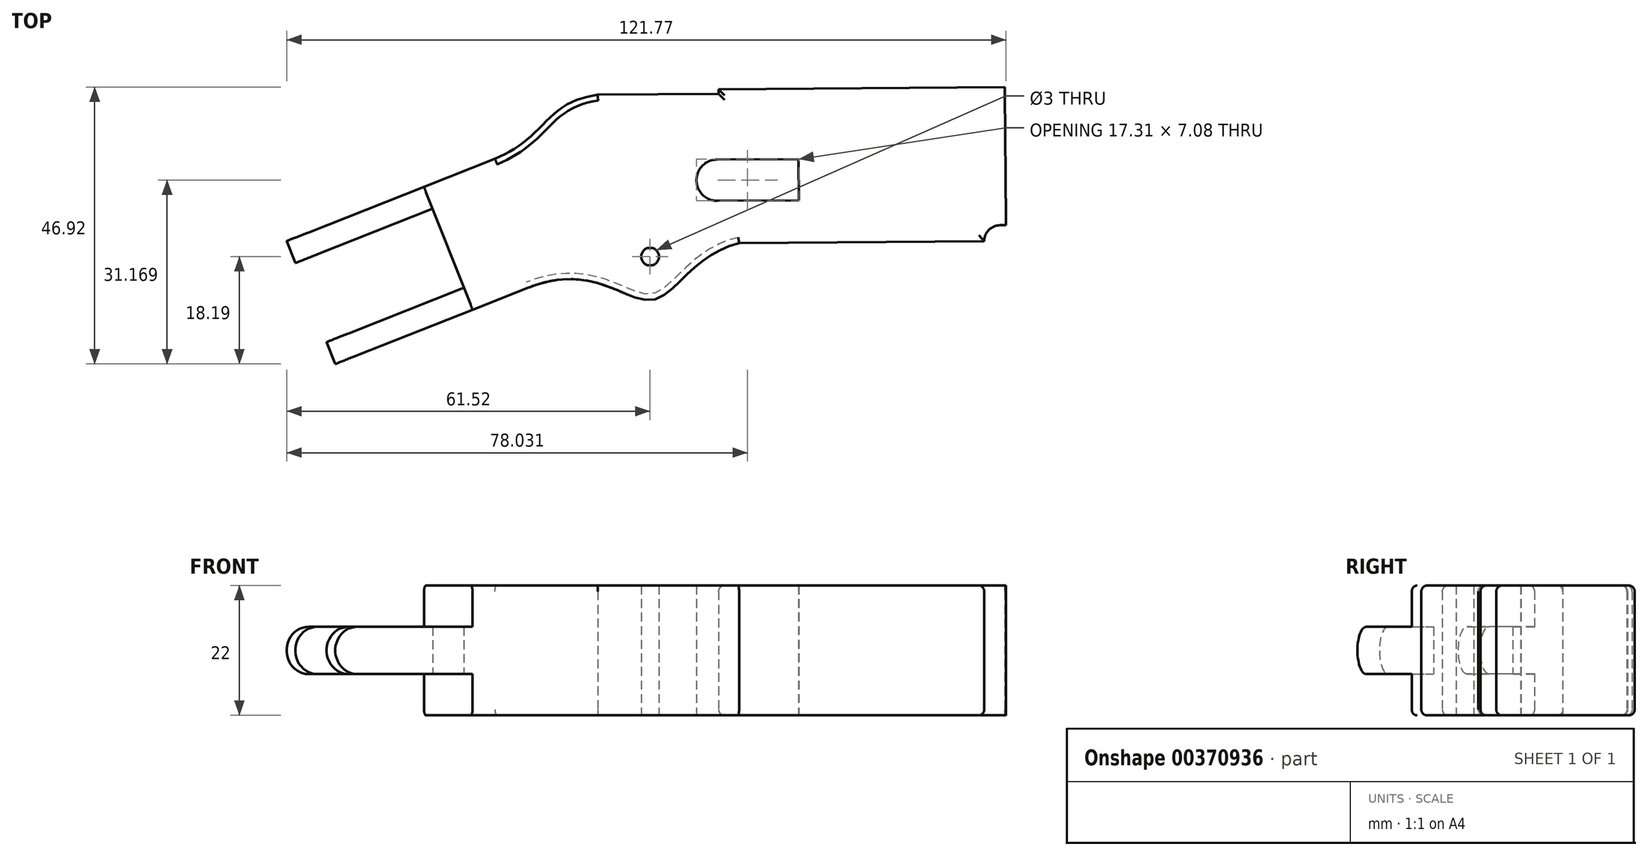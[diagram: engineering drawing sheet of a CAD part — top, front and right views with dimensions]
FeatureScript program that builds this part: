
annotation { "Feature Type Name" : "Feature", "Feature Type Description" : "" }
export const myFeature = defineFeature(function(context is Context, id is Id, definition is map)
    precondition{}
    {
        {
            var Q0;
            Q0=qCreatedBy(makeId("Top.planeOp"),FACE);
            var sketch = newSketch(context, id + "F0", { "sketchPlane" : qUnion([Q0])});
            skLineSegment(sketch, "E0", {"start": v(11.34, 16.45) * mm, "end": v(25.12, 16.52) * mm});
            skLineSegment(sketch, "E1", {"start": v(11.38, 9.44) * mm, "end": v(25.16, 9.51) * mm});
            skLineSegment(sketch, "E2", {"start": v(25.16, 9.51) * mm, "end": v(25.12, 16.52) * mm});
            skLineSegment(sketch, "E3", {"start": v(56.55, 2.63) * mm, "end": v(15.06, 2.27) * mm});
            skLineSegment(sketch, "E4", {"start": v(60.05, 28.73) * mm, "end": v(60.25, 5.31) * mm});
            skLineSegment(sketch, "E5", {"start": v(60.25, 5.31) * mm, "end": v(59.23, 5.3) * mm});
            skLineSegment(sketch, "E6", {"start": v(60.05, 28.73) * mm, "end": v(11.61, 28.3) * mm});
            skLineSegment(sketch, "E7", {"start": v(11.61, 28.3) * mm, "end": v(11.6, 27.54) * mm});
            skLineSegment(sketch, "E8", {"start": v(11.6, 27.54) * mm, "end": v(-8.88, 27.43) * mm});
            skArc(sketch, "E9", {"start": v(11.34, 16.45) * mm, "mid": v(7.86, 12.92) * mm, "end": v(11.38, 9.44) * mm});
            skFitSpline(sketch, "E10", {"points": [v(-8.88, 27.43) * mm, v(-26.26, 16.57) * mm], "startDerivative": vector(-27.72, -4.3) * mm, "endDerivative": vector(-26.55, -10.8) * mm});
            skCircle(sketch, "E11", {"center": v(0, 0) * mm, "radius": 1.5 * mm});
            skFitSpline(sketch, "E12", {"points": [v(15.06, 2.27) * mm, v(0.4, -7.32) * mm, v(-20.64, -5.27) * mm], "startDerivative": vector(-48.52, -11.19) * mm, "endDerivative": vector(-63.37, -25.45) * mm});
            skArc(sketch, "E13", {"start": v(59.23, 5.3) * mm, "mid": v(57.34, 4.51) * mm, "end": v(56.55, 2.63) * mm});
            skLineSegment(sketch, "E14", {"start": v(-20.64, -5.27) * mm, "end": v(-53.3, -18.19) * mm});
            skLineSegment(sketch, "E15", {"start": v(-61.52, 2.62) * mm, "end": v(-26.26, 16.57) * mm});
            skLineSegment(sketch, "E16", {"start": v(-61.52, 2.62) * mm, "end": v(-60.05, -1.1) * mm});
            skLineSegment(sketch, "E17", {"start": v(-53.3, -18.19) * mm, "end": v(-54.76, -14.47) * mm});
            skLineSegment(sketch, "E18", {"start": v(-60.05, -1.1) * mm, "end": v(-36.8, 8.1) * mm});
            skLineSegment(sketch, "E19", {"start": v(-36.8, 8.1) * mm, "end": v(-31.51, -5.27) * mm});
            skLineSegment(sketch, "E20", {"start": v(-31.51, -5.27) * mm, "end": v(-54.76, -14.47) * mm});
            skSolve(sketch);
        }
        {
            var Q0;
            Q0 = qSketchRegion(id + "F0", true);
            extrude(context, id + "F1", {"entities" : qUnion([Q0]), "endBound" : BoundingType.SYMMETRIC, "depth" : 22 * mm});
        }
        {
            var Q0;
            Q0=makeQuery(id+"F1.opExtrude","SWEPT_FACE",FACE,{"disambiguationData":[OSD([sQuery(id+"F0.wireOp",EDGE,"E15")])]});
            var sketch = newSketch(context, id + "F2", { "sketchPlane" : qUnion([Q0])});
            skLineSegment(sketch, "E21", {"start": v(56.24, 0) * mm, "end": v(31.24, 0) * mm, "construction": true});
            skLineSegment(sketch, "E22", {"start": v(31.24, -11.04) * mm, "end": v(31.24, 11.03) * mm});
            skLineSegment(sketch, "E23", {"start": v(31.24, -4) * mm, "end": v(52.24, -4) * mm});
            skArc(sketch, "E24", {"start": v(52.24, -4) * mm, "mid": v(55.07, -2.83) * mm, "end": v(56.24, 0) * mm});
            skLineSegment(sketch, "E25.MirrorCS", {"start": v(31.24, 4) * mm, "end": v(52.24, 4) * mm});
            skArc(sketch, "E26.MirrorCS", {"start": v(52.24, 4) * mm, "mid": v(55.07, 2.83) * mm, "end": v(56.24, 0) * mm});
            skSolve(sketch);
        }
        {
            var Q0;
            {var subQ5=sQuery(id+"F2.wireOp",EDGE,"E23");Q0=makeQuery(id+"F2.imprint","IMPRINT",FACE,{"disambiguationData":[TD([[makeQuery(id+"F2.imprint","IMPRINT",EDGE,{"derivedFrom":subQ5}),-1.0]])]});}
            var Q1;
            {var subQ5=sQuery(id+"F2.wireOp",EDGE,"E25.MirrorCS");Q1=makeQuery(id+"F2.imprint","IMPRINT",FACE,{"disambiguationData":[TD([[makeQuery(id+"F2.imprint","IMPRINT",EDGE,{"derivedFrom":subQ5}),1.0]])]});}
            extrude(context, id + "F3", {"entities" : qUnion([Q0, Q1]), "operationType" : NewBodyOperationType.REMOVE, "endBound" : BoundingType.THROUGH_ALL, "oppositeDirection" : true, "depth" : 25 * mm});
        }
        {
            var Q0;
            Q0=makeQuery(id+"F1.opExtrude","CAP_EDGE",EDGE,{"disambiguationData":[OSD([sQuery(id+"F0.wireOp",EDGE,"E6")])],"isStart":false});
            var Q1;
            Q1=makeQuery(id+"F1.opExtrude","CAP_EDGE",EDGE,{"disambiguationData":[OSD([sQuery(id+"F0.wireOp",EDGE,"E7")])],"isStart":false});
            var Q2;
            Q2=makeQuery(id+"F1.opExtrude","CAP_EDGE",EDGE,{"disambiguationData":[OSD([sQuery(id+"F0.wireOp",EDGE,"E8")])],"isStart":false});
            var Q3;
            Q3=makeQuery(id+"F1.opExtrude","CAP_EDGE",EDGE,{"disambiguationData":[OSD([sQuery(id+"F0.wireOp",EDGE,"E5")])],"isStart":false});
            var Q4;
            Q4=makeQuery(id+"F1.opExtrude","CAP_EDGE",EDGE,{"disambiguationData":[OSD([sQuery(id+"F0.wireOp",EDGE,"c1442275-6ccb-495c-8459-2948258a4f5a")])],"isStart":false});
            var Q5;
            Q5=makeQuery(id+"F1.opExtrude","CAP_EDGE",EDGE,{"disambiguationData":[OSD([sQuery(id+"F0.wireOp",EDGE,"d78f94e8-ab1f-441a-b5cc-7f1f7782cbfb")])],"isStart":false});
            var Q6;
            Q6=makeQuery(id+"F1.opExtrude","CAP_EDGE",EDGE,{"disambiguationData":[OSD([sQuery(id+"F0.wireOp",EDGE,"45dad5e2-cd43-4a6b-97fa-0e10727c4040")])],"isStart":false});
            var Q7;
            Q7=makeQuery(id+"F1.opExtrude","CAP_EDGE",EDGE,{"disambiguationData":[OSD([sQuery(id+"F0.wireOp",EDGE,"d892c378-95f4-4576-9e95-562203b950b6")])],"isStart":false});
            var Q8;
            Q8=makeQuery(id+"F1.opExtrude","CAP_EDGE",EDGE,{"disambiguationData":[OSD([sQuery(id+"F0.wireOp",EDGE,"57c3e8d9-549f-419a-a75d-53b0580d8868")])],"isStart":false});
            var Q9;
            Q9=makeQuery(id+"F1.opExtrude","CAP_EDGE",EDGE,{"disambiguationData":[OSD([sQuery(id+"F0.wireOp",EDGE,"adcbbdc1-0f74-4cde-a101-bf1f96f1e046")])],"isStart":false});
            var Q10;
            Q10=makeQuery(id+"F1.opExtrude","CAP_EDGE",EDGE,{"disambiguationData":[OSD([sQuery(id+"F0.wireOp",EDGE,"E8")])],"isStart":true});
            var Q11;
            Q11=makeQuery(id+"F1.opExtrude","CAP_EDGE",EDGE,{"disambiguationData":[OSD([sQuery(id+"F0.wireOp",EDGE,"E7")])],"isStart":true});
            var Q12;
            Q12=makeQuery(id+"F1.opExtrude","CAP_EDGE",EDGE,{"disambiguationData":[OSD([sQuery(id+"F0.wireOp",EDGE,"E6")])],"isStart":true});
            var Q13;
            Q13=makeQuery(id+"F1.opExtrude","CAP_EDGE",EDGE,{"disambiguationData":[OSD([sQuery(id+"F0.wireOp",EDGE,"45dad5e2-cd43-4a6b-97fa-0e10727c4040")])],"isStart":true});
            var Q14;
            Q14=makeQuery(id+"F1.opExtrude","CAP_EDGE",EDGE,{"disambiguationData":[OSD([sQuery(id+"F0.wireOp",EDGE,"d892c378-95f4-4576-9e95-562203b950b6")])],"isStart":true});
            var Q15;
            Q15=makeQuery(id+"F1.opExtrude","CAP_EDGE",EDGE,{"disambiguationData":[OSD([sQuery(id+"F0.wireOp",EDGE,"57c3e8d9-549f-419a-a75d-53b0580d8868")])],"isStart":true});
            var Q16;
            Q16=makeQuery(id+"F1.opExtrude","CAP_EDGE",EDGE,{"disambiguationData":[OSD([sQuery(id+"F0.wireOp",EDGE,"c1442275-6ccb-495c-8459-2948258a4f5a")])],"isStart":true});
            var Q17;
            Q17=makeQuery(id+"F1.opExtrude","CAP_EDGE",EDGE,{"disambiguationData":[OSD([sQuery(id+"F0.wireOp",EDGE,"E5")])],"isStart":true});
            var Q18;
            Q18=makeQuery(id+"F1.opExtrude","CAP_EDGE",EDGE,{"disambiguationData":[OSD([sQuery(id+"F0.wireOp",EDGE,"d78f94e8-ab1f-441a-b5cc-7f1f7782cbfb")])],"isStart":true});
            var Q19;
            Q19=makeQuery(id+"F1.opExtrude","CAP_EDGE",EDGE,{"disambiguationData":[OSD([sQuery(id+"F0.wireOp",EDGE,"adcbbdc1-0f74-4cde-a101-bf1f96f1e046")])],"isStart":true});
            var Q20;
            Q20=makeQuery(id+"F1.opExtrude","CAP_EDGE",EDGE,{"disambiguationData":[OSD([sQuery(id+"F0.wireOp",EDGE,"E10")])],"isStart":false});
            var Q21;
            Q21=makeQuery(id+"F1.opExtrude","CAP_EDGE",EDGE,{"disambiguationData":[OSD([sQuery(id+"F0.wireOp",EDGE,"E10")])],"isStart":true});
            var Q22;
            Q22=makeQuery(id+"F1.opExtrude","CAP_EDGE",EDGE,{"disambiguationData":[OSD([sQuery(id+"F0.wireOp",EDGE,"6784bd22-df8c-4650-9e87-a9f711e7ee04")])],"isStart":false});
            var Q23;
            Q23=makeQuery(id+"F1.opExtrude","CAP_EDGE",EDGE,{"disambiguationData":[OSD([sQuery(id+"F0.wireOp",EDGE,"6784bd22-df8c-4650-9e87-a9f711e7ee04")])],"isStart":true});
            var Q24;
            Q24=makeQuery(id+"F1.opExtrude","CAP_EDGE",EDGE,{"disambiguationData":[OSD([sQuery(id+"F0.wireOp",EDGE,"1d94e01c-a320-4d41-bd32-02b2e2ef5809")])],"isStart":false});
            var Q25;
            Q25=makeQuery(id+"F1.opExtrude","CAP_EDGE",EDGE,{"disambiguationData":[OSD([sQuery(id+"F0.wireOp",EDGE,"1d94e01c-a320-4d41-bd32-02b2e2ef5809")])],"isStart":true});
            var Q26;
            Q26=makeQuery(id+"F1.opExtrude","CAP_EDGE",EDGE,{"disambiguationData":[OSD([sQuery(id+"F0.wireOp",EDGE,"457901ba-0a1f-4618-be23-e307e29b51c9")])],"isStart":false});
            var Q27;
            Q27=makeQuery(id+"F1.opExtrude","CAP_EDGE",EDGE,{"disambiguationData":[OSD([sQuery(id+"F0.wireOp",EDGE,"da8b7c37-8d01-4374-8bd5-a513392d17b2")])],"isStart":false});
            var Q28;
            Q28=makeQuery(id+"F1.opExtrude","CAP_EDGE",EDGE,{"disambiguationData":[OSD([sQuery(id+"F0.wireOp",EDGE,"E3")])],"isStart":false});
            var Q29;
            Q29=makeQuery(id+"F1.opExtrude","CAP_EDGE",EDGE,{"disambiguationData":[OSD([sQuery(id+"F0.wireOp",EDGE,"E3")])],"isStart":true});
            var Q30;
            Q30=makeQuery(id+"F1.opExtrude","CAP_EDGE",EDGE,{"disambiguationData":[OSD([sQuery(id+"F0.wireOp",EDGE,"E12")])],"isStart":true});
            var Q31;
            Q31=makeQuery(id+"F1.opExtrude","CAP_EDGE",EDGE,{"disambiguationData":[OSD([sQuery(id+"F0.wireOp",EDGE,"da8b7c37-8d01-4374-8bd5-a513392d17b2")])],"isStart":true});
            var Q32;
            Q32=makeQuery(id+"F1.opExtrude","CAP_EDGE",EDGE,{"disambiguationData":[OSD([sQuery(id+"F0.wireOp",EDGE,"457901ba-0a1f-4618-be23-e307e29b51c9")])],"isStart":true});
            var Q33;
            Q33=makeQuery(id+"F1.opExtrude","CAP_EDGE",EDGE,{"disambiguationData":[OSD([sQuery(id+"F0.wireOp",EDGE,"E12")])],"isStart":false});
            var Q34;
            Q34=makeQuery(id+"F1.opExtrude","CAP_EDGE",EDGE,{"disambiguationData":[OSD([sQuery(id+"F0.wireOp",EDGE,"E14")])],"isStart":false});
            var Q35;
            Q35=makeQuery(id+"F1.opExtrude","CAP_EDGE",EDGE,{"disambiguationData":[OSD([sQuery(id+"F0.wireOp",EDGE,"E15")])],"isStart":false});
            var Q36;
            Q36=makeQuery(id+"F1.opExtrude","CAP_EDGE",EDGE,{"disambiguationData":[OSD([sQuery(id+"F0.wireOp",EDGE,"E14")])],"isStart":true});
            var Q37;
            Q37=makeQuery(id+"F1.opExtrude","CAP_EDGE",EDGE,{"disambiguationData":[OSD([sQuery(id+"F0.wireOp",EDGE,"E13")])],"isStart":true});
            var Q38;
            Q38=makeQuery(id+"F1.opExtrude","CAP_EDGE",EDGE,{"disambiguationData":[OSD([sQuery(id+"F0.wireOp",EDGE,"E15")])],"isStart":true});
            fillet(context, id + "F4", {"entities" : qUnion([Q0, Q1, Q2, Q3, Q4, Q5, Q6, Q7, Q8, Q9, Q10, Q11, Q12, Q13, Q14, Q15, Q16, Q17, Q18, Q19, Q20, Q21, Q22, Q23, Q24, Q25, Q26, Q27, Q28, Q29, Q30, Q31, Q32, Q33, Q34, Q35, Q36, Q37, Q38]), "radius" : 1 * mm, "tangentPropagation" : true, "allowEdgeOverflow" : false});
        }
    });
